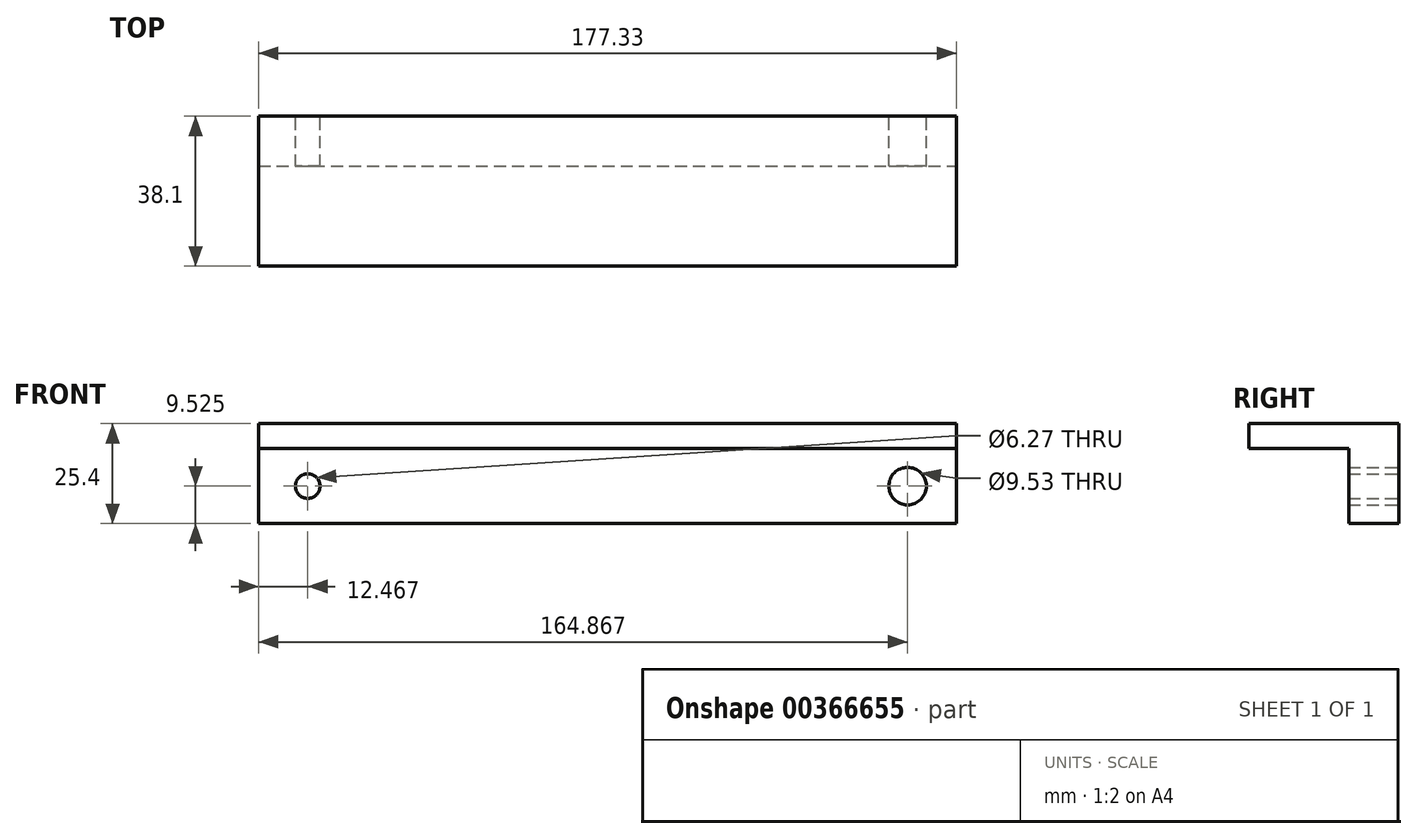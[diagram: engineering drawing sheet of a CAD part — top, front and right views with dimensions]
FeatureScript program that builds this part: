
annotation { "Feature Type Name" : "Feature", "Feature Type Description" : "" }
export const myFeature = defineFeature(function(context is Context, id is Id, definition is map)
    precondition{}
    {
        {
            var Q0;
            Q0=qCreatedBy(makeId("Front.planeOp"),FACE);
            var sketch = newSketch(context, id + "F0", { "sketchPlane" : qUnion([Q0])});
            skLineSegment(sketch, "E0.bottom", {"start": v(0, 0) * mm, "end": v(177.33, 0) * mm});
            skLineSegment(sketch, "E0.top", {"start": v(0, 19.05) * mm, "end": v(177.33, 19.05) * mm});
            skLineSegment(sketch, "E0.left", {"start": v(0, 0) * mm, "end": v(0, 19.05) * mm});
            skLineSegment(sketch, "E0.right", {"start": v(177.33, 0) * mm, "end": v(177.33, 19.05) * mm});
            skCircle(sketch, "E1", {"center": v(12.47, 9.53) * mm, "radius": 3.14 * mm});
            skPoint(sketch, "E1.centerSnap0", {"position": v(0, 9.53) * mm});
            skCircle(sketch, "E2", {"center": v(164.87, 9.53) * mm, "radius": 4.76 * mm});
            skSolve(sketch);
        }
        {
            var Q0;
            Q0=makeQuery(id+"F0.imprint","IMPRINT",FACE,{"disambiguationData":[TD([[makeQuery(id+"F0.imprint","IMPRINT",EDGE,{"derivedFrom":sQuery(id+"F0.wireOp",EDGE,"E0.bottom")}),1.0]])]});
            extrude(context, id + "F1", {"entities" : qUnion([Q0]), "depth" : 12.7 * mm});
        }
        {
            var Q0;
            Q0=makeQuery(id+"F1.opExtrude","CAP_FACE",FACE,{"disambiguationData":[OSD([sQuery(id+"F0.wireOp",EDGE,"E0.bottom"),sQuery(id+"F0.wireOp",EDGE,"E0.top"),sQuery(id+"F0.wireOp",EDGE,"E0.left"),sQuery(id+"F0.wireOp",EDGE,"E0.right"),sQuery(id+"F0.wireOp",EDGE,"E1"),sQuery(id+"F0.wireOp",EDGE,"E2")])],"isStart":false});
            var sketch = newSketch(context, id + "F2", { "sketchPlane" : qUnion([Q0])});
            skLineSegment(sketch, "E3.0", {"start": v(0, 19.05) * mm, "end": v(177.33, 19.05) * mm});
            skLineSegment(sketch, "E4", {"start": v(0, 19.05) * mm, "end": v(0, 25.4) * mm});
            skLineSegment(sketch, "E5", {"start": v(0, 25.4) * mm, "end": v(177.33, 25.4) * mm});
            skLineSegment(sketch, "E6", {"start": v(177.33, 19.05) * mm, "end": v(177.33, 25.4) * mm});
            skSolve(sketch);
        }
        {
            var Q0;
            Q0 = qSketchRegion(id + "F2", true);
            var Q1;
            Q1=makeQuery(id+"F1.opExtrude","CAP_FACE",FACE,{"disambiguationData":[OSD([sQuery(id+"F0.wireOp",EDGE,"E0.bottom"),sQuery(id+"F0.wireOp",EDGE,"E0.top"),sQuery(id+"F0.wireOp",EDGE,"E0.left"),sQuery(id+"F0.wireOp",EDGE,"E0.right"),sQuery(id+"F0.wireOp",EDGE,"E1"),sQuery(id+"F0.wireOp",EDGE,"E2")])],"isStart":true});
            extrude(context, id + "F3", {"entities" : qUnion([Q0]), "operationType" : NewBodyOperationType.ADD, "depth" : 25.4 * mm, "hasSecondDirection" : true, "secondDirectionBound" : SecondDirectionBoundingType.UP_TO_SURFACE, "secondDirectionOppositeDirection" : true, "secondDirectionBoundEntityFace" : qUnion([Q1]), "secondDirectionDepth" : 25.4 * mm});
        }
    });
